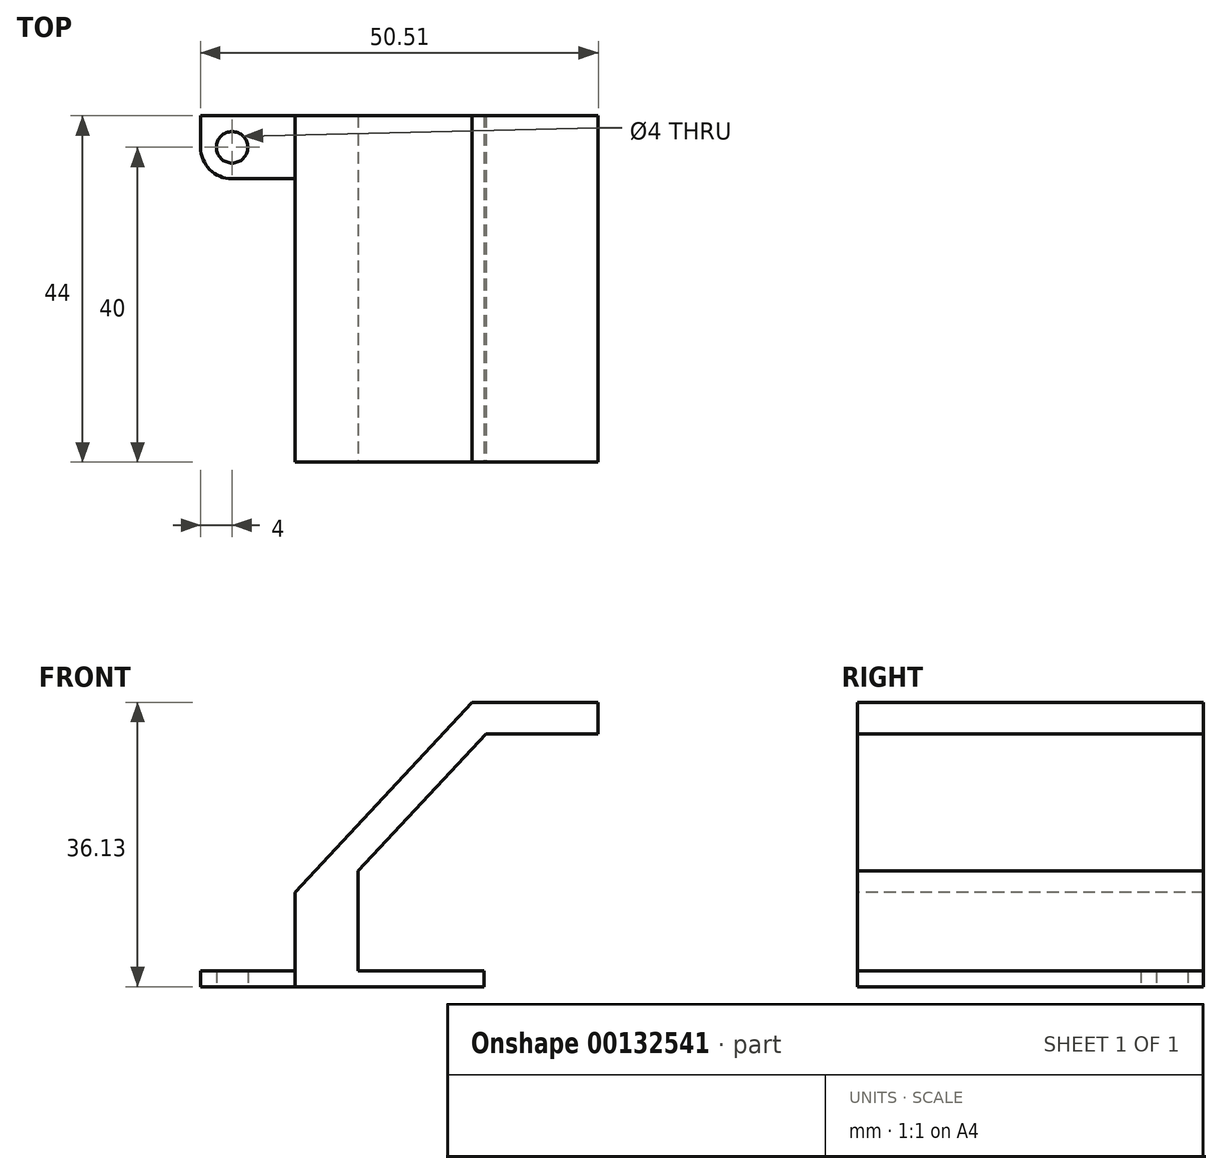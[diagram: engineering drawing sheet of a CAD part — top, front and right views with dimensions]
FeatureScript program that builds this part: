
annotation { "Feature Type Name" : "Feature", "Feature Type Description" : "" }
export const myFeature = defineFeature(function(context is Context, id is Id, definition is map)
    precondition{}
    {
        {
            var Q0;
            Q0=qCreatedBy(makeId("Front.planeOp"),FACE);
            var sketch = newSketch(context, id + "F0", { "sketchPlane" : qUnion([Q0])});
            skLineSegment(sketch, "E0", {"start": v(0, 0) * mm, "end": v(0, 2) * mm});
            skLineSegment(sketch, "E1", {"start": v(0, 2) * mm, "end": v(12, 2) * mm});
            skLineSegment(sketch, "E2", {"start": v(12, 2) * mm, "end": v(12, 12) * mm});
            skLineSegment(sketch, "E3", {"start": v(12, 12) * mm, "end": v(34.5, 36.13) * mm});
            skLineSegment(sketch, "E4", {"start": v(34.5, 36.13) * mm, "end": v(50.5, 36.13) * mm});
            skLineSegment(sketch, "E5", {"start": v(50.5, 36.13) * mm, "end": v(50.5, 32.13) * mm});
            skLineSegment(sketch, "E6", {"start": v(50.5, 32.13) * mm, "end": v(36.25, 32.13) * mm});
            skLineSegment(sketch, "E7", {"start": v(36.25, 32.13) * mm, "end": v(20, 14.71) * mm});
            skLineSegment(sketch, "E8", {"start": v(20, 14.71) * mm, "end": v(20, 2) * mm});
            skLineSegment(sketch, "E9", {"start": v(20, 2) * mm, "end": v(36, 2) * mm});
            skLineSegment(sketch, "E10", {"start": v(36, 2) * mm, "end": v(36, 0) * mm});
            skLineSegment(sketch, "E11", {"start": v(36, 0) * mm, "end": v(0, 0) * mm});
            skLineSegment(sketch, "E12", {"start": v(20, 14.71) * mm, "end": v(38.1, 14.71) * mm, "construction": true});
            skSolve(sketch);
        }
        {
            var Q0;
            Q0 = qSketchRegion(id + "F0", true);
            extrude(context, id + "F1", {"entities" : qUnion([Q0]), "oppositeDirection" : true, "depth" : 44 * mm});
        }
        {
            var Q0;
            Q0=qCreatedBy(makeId("Top.planeOp"),FACE);
            var sketch = newSketch(context, id + "F2", { "sketchPlane" : qUnion([Q0])});
            skCircle(sketch, "E13", {"center": v(4, 40) * mm, "radius": 2 * mm});
            skLineSegment(sketch, "E14.0", {"start": v(12, 44) * mm, "end": v(12, 0) * mm});
            skLineSegment(sketch, "E15", {"start": v(4, 36) * mm, "end": v(12, 36) * mm});
            skLineSegment(sketch, "E16.0", {"start": v(0, 44) * mm, "end": v(0, 0) * mm});
            skLineSegment(sketch, "E17.0", {"start": v(0, 0) * mm, "end": v(12, 0) * mm});
            skArc(sketch, "E18", {"start": v(4, 36) * mm, "mid": v(0, 40) * mm, "end": v(4, 44) * mm});
            skSolve(sketch);
        }
        {
            var Q0;
            Q0 = qSketchRegion(id + "F2", true);
            extrude(context, id + "F3", {"entities" : qUnion([Q0]), "operationType" : NewBodyOperationType.REMOVE, "depth" : 25 * mm});
        }
    });
